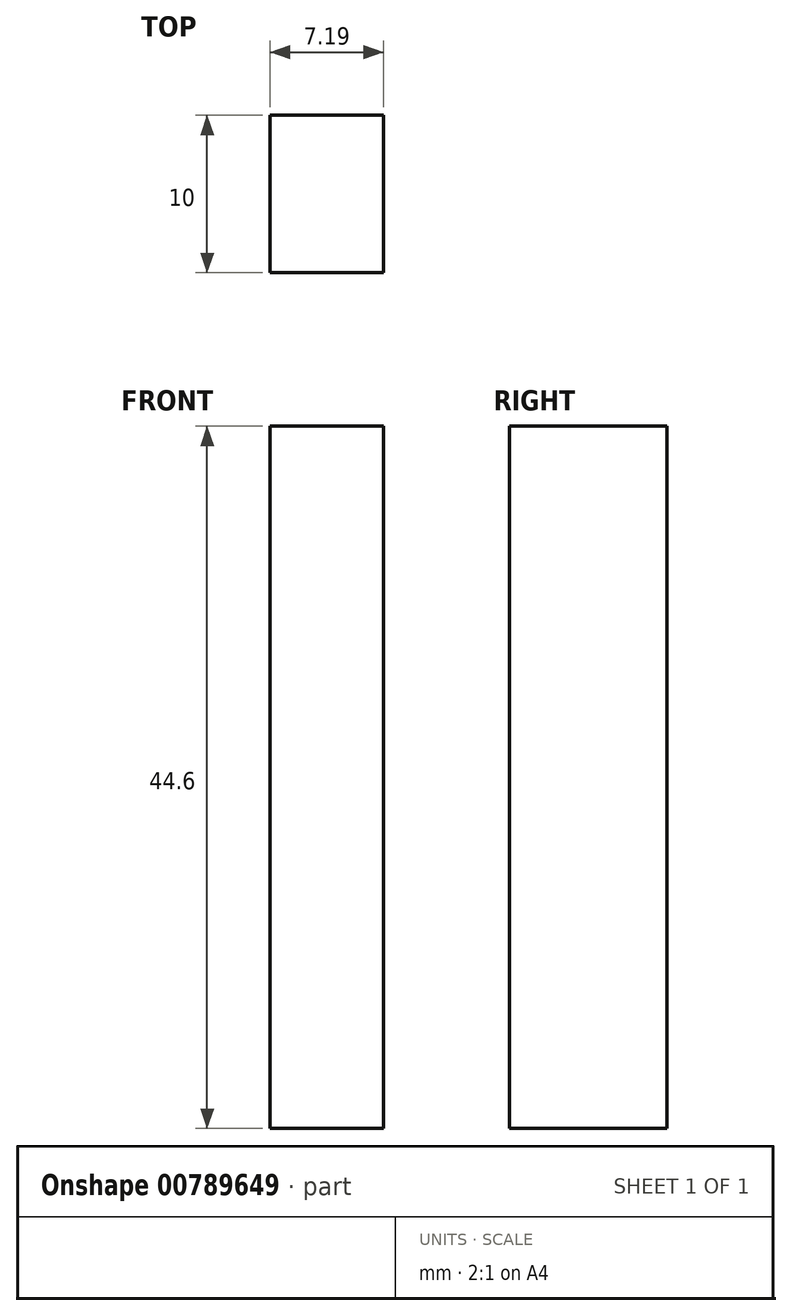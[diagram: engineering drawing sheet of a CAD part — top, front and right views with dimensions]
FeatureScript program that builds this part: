
annotation { "Feature Type Name" : "Feature", "Feature Type Description" : "" }
export const myFeature = defineFeature(function(context is Context, id is Id, definition is map)
    precondition{}
    {
        {
            var Q0;
            Q0=qCreatedBy(makeId("Top.planeOp"),FACE);
            var sketch = newSketch(context, id + "F0", { "sketchPlane" : qUnion([Q0])});
            skLineSegment(sketch, "E0.bottom", {"start": v(0, 10) * mm, "end": v(7.2, 10) * mm});
            skLineSegment(sketch, "E0.top", {"start": v(0, 0) * mm, "end": v(7.2, 0) * mm});
            skLineSegment(sketch, "E0.left", {"start": v(0, 10) * mm, "end": v(0, 0) * mm});
            skLineSegment(sketch, "E0.right", {"start": v(7.2, 10) * mm, "end": v(7.2, 0) * mm});
            skSolve(sketch);
        }
        {
            var Q0;
            Q0=makeQuery(id+"F0.imprint","IMPRINT",FACE,{"disambiguationData":[TD([[makeQuery(id+"F0.imprint","IMPRINT",EDGE,{"derivedFrom":sQuery(id+"F0.wireOp",EDGE,"E0.bottom")}),-1.0]])]});
            extrude(context, id + "F1", {"entities" : qUnion([Q0]), "depth" : 44.6 * mm, "offsetDistance" : 25 * mm});
        }
    });
